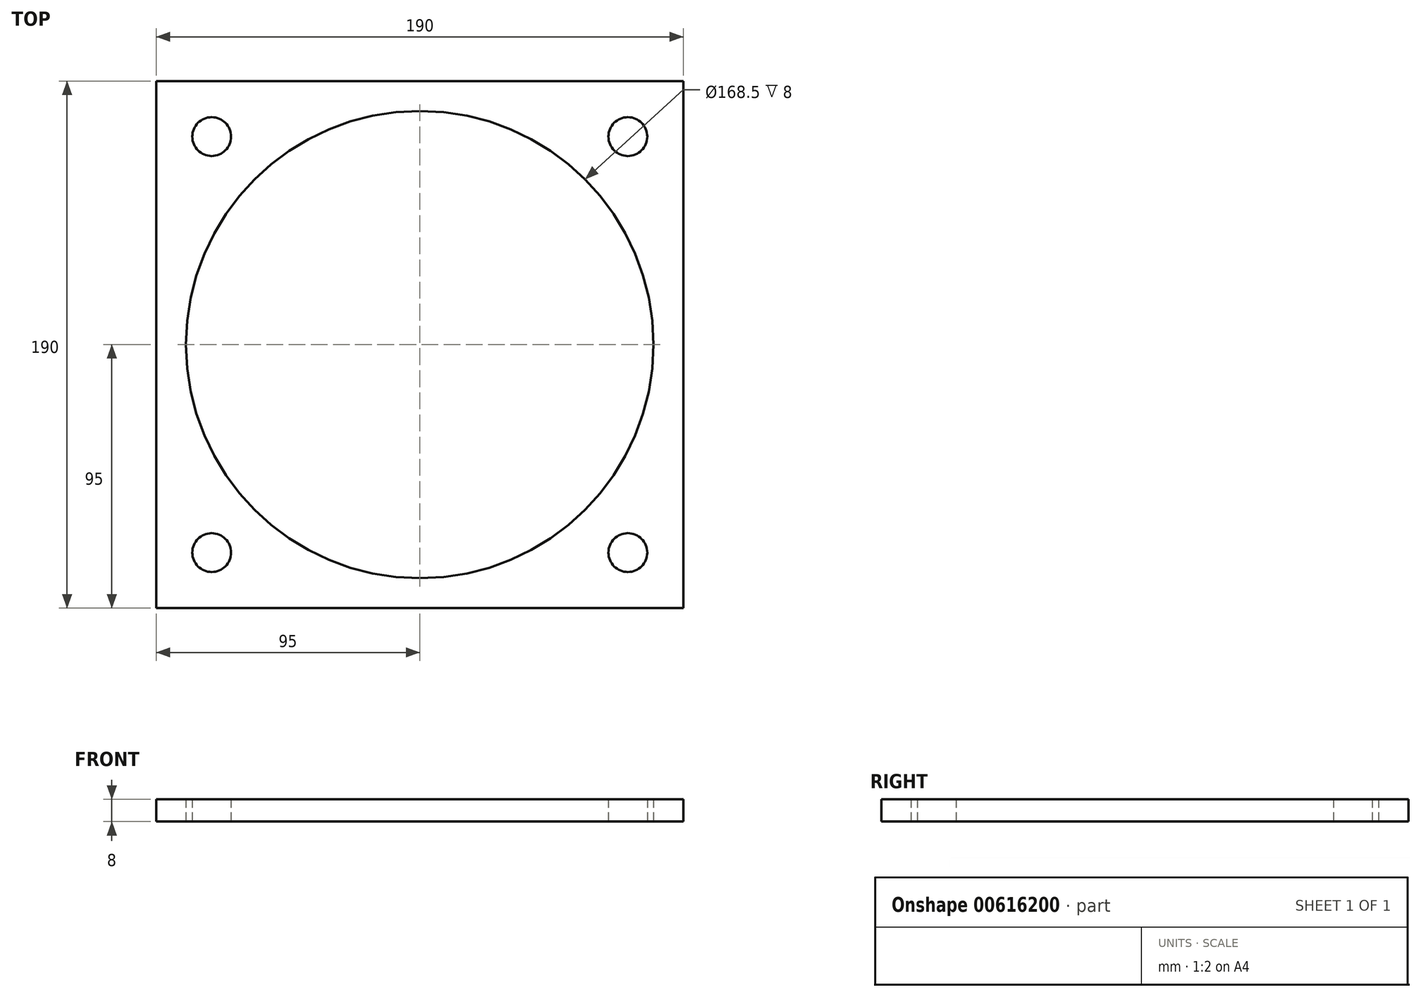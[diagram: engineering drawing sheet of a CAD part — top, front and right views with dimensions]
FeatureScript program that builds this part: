
annotation { "Feature Type Name" : "Feature", "Feature Type Description" : "" }
export const myFeature = defineFeature(function(context is Context, id is Id, definition is map)
    precondition{}
    {
        {
            var Q0;
            Q0=qCreatedBy(makeId("Top.planeOp"),FACE);
            var sketch = newSketch(context, id + "F0", { "sketchPlane" : qUnion([Q0])});
            skLineSegment(sketch, "E0.bottom", {"start": v(-95, -95) * mm, "end": v(95, -95) * mm});
            skLineSegment(sketch, "E0.top", {"start": v(-95, 95) * mm, "end": v(95, 95) * mm});
            skLineSegment(sketch, "E0.left", {"start": v(-95, -95) * mm, "end": v(-95, 95) * mm});
            skLineSegment(sketch, "E0.right", {"start": v(95, -95) * mm, "end": v(95, 95) * mm});
            skPoint(sketch, "E0.middle", {"position": v(0, 0) * mm});
            skCircle(sketch, "E1", {"center": v(0, 0) * mm, "radius": 84.25 * mm});
            skCircle(sketch, "E2", {"center": v(-75, 75) * mm, "radius": 7 * mm});
            skCircle(sketch, "E3", {"center": v(75, 75) * mm, "radius": 7 * mm});
            skCircle(sketch, "E4", {"center": v(-75, -75) * mm, "radius": 7 * mm});
            skCircle(sketch, "E5", {"center": v(75, -75) * mm, "radius": 7 * mm});
            skSolve(sketch);
        }
        {
            var Q0;
            Q0 = qSketchRegion(id + "F0", true);
            extrude(context, id + "F1", {"entities" : qUnion([Q0]), "depth" : 8 * mm, "offsetDistance" : 25 * mm});
        }
    });
